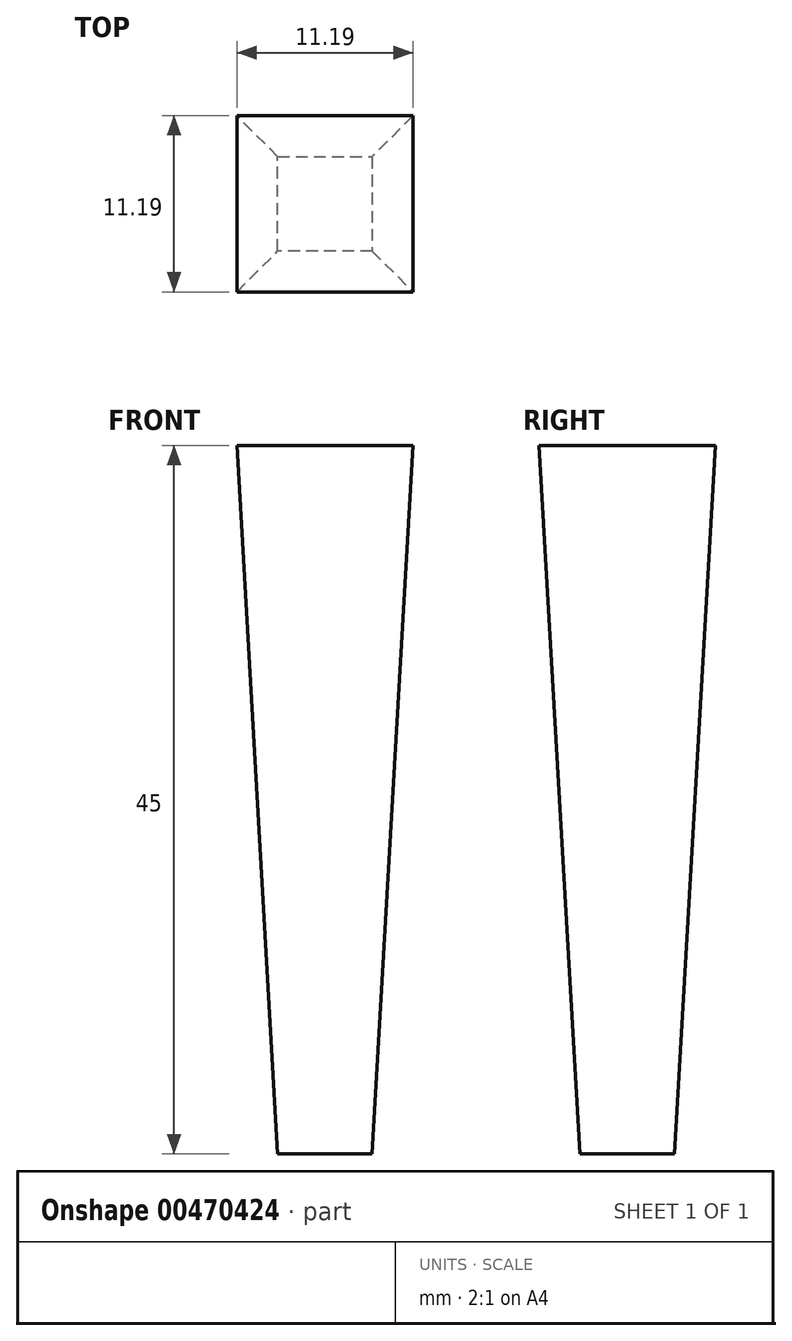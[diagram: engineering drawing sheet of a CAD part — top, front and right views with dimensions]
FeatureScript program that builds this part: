
annotation { "Feature Type Name" : "Feature", "Feature Type Description" : "" }
export const myFeature = defineFeature(function(context is Context, id is Id, definition is map)
    precondition{}
    {
        {
            var Q0;
            Q0=qCreatedBy(makeId("Top.planeOp"),FACE);
            var sketch = newSketch(context, id + "F0", { "sketchPlane" : qUnion([Q0])});
            skLineSegment(sketch, "E0.bottom", {"start": v(-32.09, -4.56) * mm, "end": v(-26.09, -4.56) * mm});
            skLineSegment(sketch, "E0.top", {"start": v(-32.09, -10.56) * mm, "end": v(-26.09, -10.56) * mm});
            skLineSegment(sketch, "E0.left", {"start": v(-32.09, -4.56) * mm, "end": v(-32.09, -10.56) * mm});
            skLineSegment(sketch, "E0.right", {"start": v(-26.09, -4.56) * mm, "end": v(-26.09, -10.56) * mm});
            skSolve(sketch);
        }
        {
            var Q0;
            Q0 = qSketchRegion(id + "F0", true);
            extrude(context, id + "F1", {"entities" : qUnion([Q0]), "depth" : 45 * mm, "hasDraft" : true, "draftAngle" : 3.3 * degree});
        }
    });
